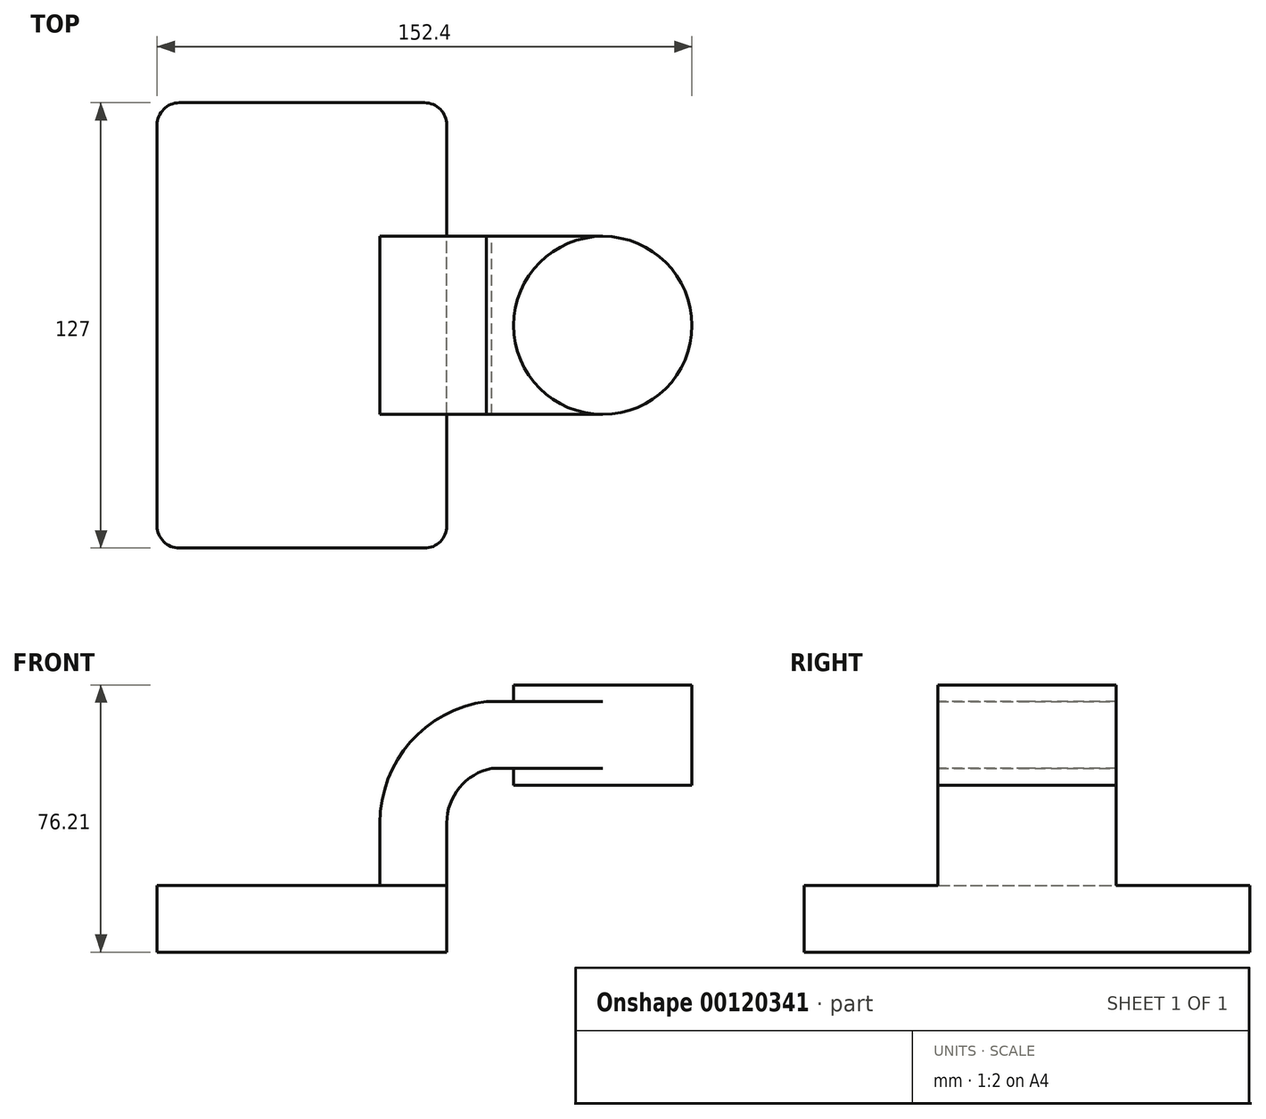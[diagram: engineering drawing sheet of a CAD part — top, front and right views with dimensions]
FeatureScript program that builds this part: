
annotation { "Feature Type Name" : "Feature", "Feature Type Description" : "" }
export const myFeature = defineFeature(function(context is Context, id is Id, definition is map)
    precondition{}
    {
        {
            var Q0;
            Q0=qCreatedBy(makeId("Front.planeOp"),FACE);
            var sketch = newSketch(context, id + "F0", { "sketchPlane" : qUnion([Q0])});
            skLineSegment(sketch, "E0.bottom", {"start": v(-41.27, -9.53) * mm, "end": v(41.28, -9.53) * mm});
            skLineSegment(sketch, "E0.top", {"start": v(-41.28, 9.52) * mm, "end": v(41.28, 9.52) * mm});
            skLineSegment(sketch, "E0.left", {"start": v(-41.28, -9.53) * mm, "end": v(-41.28, 9.53) * mm});
            skLineSegment(sketch, "E0.right", {"start": v(41.28, -9.53) * mm, "end": v(41.28, 9.52) * mm});
            skPoint(sketch, "E0.middle", {"position": v(0, 0) * mm});
            skLineSegment(sketch, "E1.bottom", {"start": v(60.32, 66.67) * mm, "end": v(111.12, 66.67) * mm});
            skLineSegment(sketch, "E1.top", {"start": v(60.32, 38.1) * mm, "end": v(111.12, 38.1) * mm});
            skLineSegment(sketch, "E1.left", {"start": v(60.33, 66.67) * mm, "end": v(60.32, 38.1) * mm});
            skLineSegment(sketch, "E1.right", {"start": v(111.12, 66.67) * mm, "end": v(111.12, 38.1) * mm});
            skPoint(sketch, "E1.middle", {"position": v(85.72, 52.39) * mm});
            skLineSegment(sketch, "E2", {"start": v(41.27, 9.52) * mm, "end": v(41.27, 27.3) * mm});
            skArc(sketch, "E3", {"start": v(41.27, 27.3) * mm, "mid": v(44.89, 37.38) * mm, "end": v(54.07, 42.88) * mm});
            skLineSegment(sketch, "E4", {"start": v(54.07, 42.88) * mm, "end": v(85.72, 42.88) * mm});
            skPoint(sketch, "E5", {"position": v(85.72, 38.1) * mm});
            skLineSegment(sketch, "E6.0", {"start": v(52.57, 61.93) * mm, "end": v(85.72, 61.93) * mm});
            skArc(sketch, "E6.1", {"start": v(22.23, 27.3) * mm, "mid": v(30.89, 50.32) * mm, "end": v(52.57, 61.93) * mm});
            skLineSegment(sketch, "E6.2", {"start": v(22.22, 9.52) * mm, "end": v(22.22, 27.3) * mm});
            skLineSegment(sketch, "E7", {"start": v(85.73, 42.88) * mm, "end": v(85.73, 61.93) * mm});
            skFitSpline(sketch, "E8", {"points": [v(-41.27, 9.52) * mm, v(52.57, 61.93) * mm], "startDerivative": vector(-0.43, 121.44) * mm, "endDerivative": vector(133.83, 1.07) * mm});
            skPoint(sketch, "E9", {"position": v(85.72, 66.67) * mm});
            skLineSegment(sketch, "E10", {"start": v(85.72, 61.93) * mm, "end": v(85.72, 66.67) * mm});
            skLineSegment(sketch, "E11", {"start": v(85.72, 42.88) * mm, "end": v(85.72, 38.1) * mm});
            skSolve(sketch);
        }
        {
            var Q0;
            Q0=makeQuery(id+"F0.imprint","IMPRINT",FACE,{"disambiguationData":[TD([[makeQuery(id+"F0.imprint","IMPRINT",EDGE,{"derivedFrom":sQuery(id+"F0.wireOp",EDGE,"E0.bottom")}),1.0]])]});
            extrude(context, id + "F1", {"entities" : qUnion([Q0]), "endBound" : BoundingType.SYMMETRIC, "depth" : 127 * mm});
        }
        {
            var Q0;
            {var subQ1=sQuery(id+"F0.wireOp",EDGE,"E2");Q0=makeQuery(id+"F0.imprint","IMPRINT",FACE,{"disambiguationData":[TD([[makeQuery(id+"F0.imprint","IMPRINT",EDGE,{"derivedFrom":subQ1}),1.0]])]});}
            var Q1;
            {var subQ5=sQuery(id+"F0.wireOp",EDGE,"E7");Q1=makeQuery(id+"F0.imprint","IMPRINT",FACE,{"disambiguationData":[TD([[makeQuery(id+"F0.imprint","IMPRINT",EDGE,{"derivedFrom":subQ5}),1.0]])]});}
            extrude(context, id + "F2", {"entities" : qUnion([Q0, Q1]), "operationType" : NewBodyOperationType.ADD, "endBound" : BoundingType.SYMMETRIC, "depth" : 50.8 * mm});
        }
        {
            var Q0;
            Q0=makeQuery(id+"F0.imprint","IMPRINT",FACE,{"disambiguationData":[TD([[makeQuery(id+"F0.imprint","IMPRINT",EDGE,{"derivedFrom":sQuery(id+"F0.wireOp",EDGE,"E6.1")}),1.0]])]});
            extrude(context, id + "F3", {"entities" : qUnion([Q0]), "operationType" : NewBodyOperationType.ADD, "endBound" : BoundingType.SYMMETRIC, "depth" : 15.88 * mm});
        }
        {
            var Q0;
            {var subQ0=sQuery(id+"F0.wireOp",EDGE,"E1.right");Q0=makeQuery(id+"F0.imprint","IMPRINT",FACE,{"disambiguationData":[TD([[makeQuery(id+"F0.imprint","IMPRINT",EDGE,{"derivedFrom":subQ0}),-1.0]])]});}
            var Q1;
            Q1=sQuery(id+"F0.wireOp",EDGE,"E7");
            revolve(context, id + "F4", {"operationType" : NewBodyOperationType.ADD, "entities" : qUnion([Q0]), "axis" : qUnion([Q1]), "revolveType" : RevolveType.FULL});
        }
        {
            var Q0;
            Q0=makeQuery(id+"F1.opExtrude","CAP_EDGE",EDGE,{"disambiguationData":[OSD([sQuery(id+"F0.wireOp",EDGE,"E0.left")])],"isStart":false});
            var Q1;
            Q1=makeQuery(id+"F1.opExtrude","CAP_EDGE",EDGE,{"disambiguationData":[OSD([sQuery(id+"F0.wireOp",EDGE,"E0.right")])],"isStart":false});
            var Q2;
            Q2=makeQuery(id+"F1.opExtrude","CAP_EDGE",EDGE,{"disambiguationData":[OSD([sQuery(id+"F0.wireOp",EDGE,"E0.right")])],"isStart":true});
            var Q3;
            Q3=makeQuery(id+"F1.opExtrude","CAP_EDGE",EDGE,{"disambiguationData":[OSD([sQuery(id+"F0.wireOp",EDGE,"E0.left")])],"isStart":true});
            fillet(context, id + "F5", {"entities" : qUnion([Q0, Q1, Q2, Q3]), "radius" : 6.35 * mm, "tangentPropagation" : true, "allowEdgeOverflow" : false});
        }
    });
